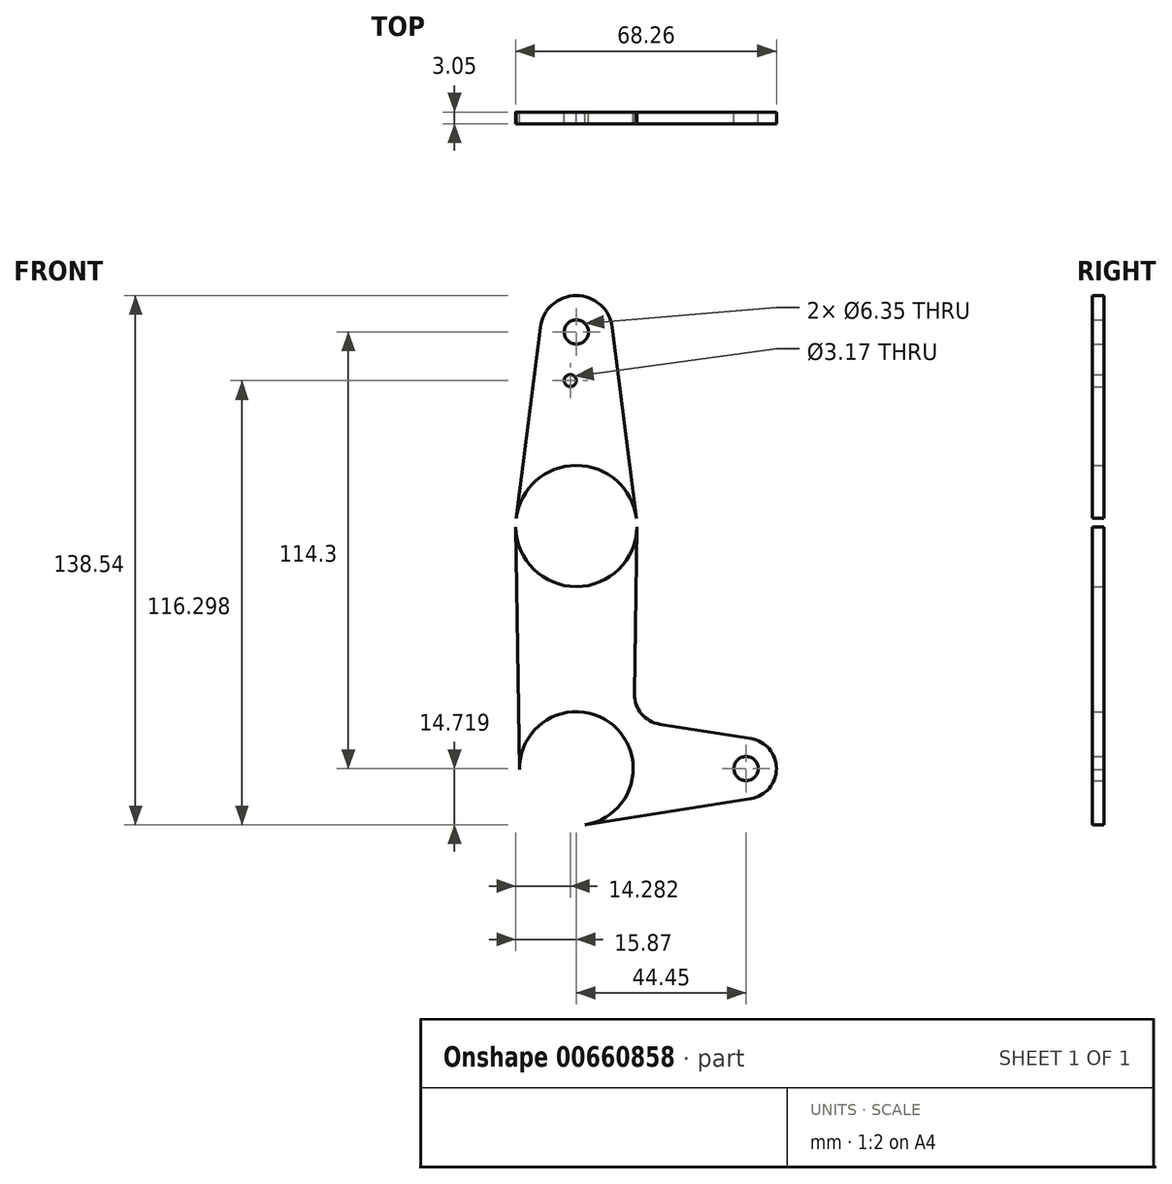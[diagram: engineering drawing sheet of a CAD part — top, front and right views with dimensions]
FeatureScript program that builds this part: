
annotation { "Feature Type Name" : "Feature", "Feature Type Description" : "" }
export const myFeature = defineFeature(function(context is Context, id is Id, definition is map)
    precondition{}
    {
        {
            var Q0;
            Q0=qCreatedBy(makeId("Front.planeOp"),FACE);
            var sketch = newSketch(context, id + "F0", { "sketchPlane" : qUnion([Q0])});
            skLineSegment(sketch, "E0", {"start": v(0, 0) * mm, "end": v(0, -57.23) * mm});
            skLineSegment(sketch, "E1", {"start": v(0, -57.23) * mm, "end": v(0, 57.07) * mm});
            skLineSegment(sketch, "E2", {"start": v(0, 57.07) * mm, "end": v(0, -57.23) * mm});
            skLineSegment(sketch, "E3", {"start": v(44.45, -57.23) * mm, "end": v(0, -57.23) * mm});
            skCircle(sketch, "E4", {"center": v(0, 6.27) * mm, "radius": 15.88 * mm});
            skCircle(sketch, "E5", {"center": v(0, 57.07) * mm, "radius": 9.53 * mm});
            skCircle(sketch, "E6", {"center": v(0, -57.23) * mm, "radius": 14.9 * mm});
            skCircle(sketch, "E7", {"center": v(44.45, -57.23) * mm, "radius": 7.94 * mm});
            skPoint(sketch, "E8.orphan", {"position": v(-60.31, 57.07) * mm});
            skLineSegment(sketch, "E9", {"start": v(9.45, 58.26) * mm, "end": v(15.75, 8.25) * mm});
            skLineSegment(sketch, "E10", {"start": v(15.87, 6.02) * mm, "end": v(15.2, -37.65) * mm});
            skLineSegment(sketch, "E11", {"start": v(-15.75, 8.25) * mm, "end": v(-9.45, 58.26) * mm});
            skLineSegment(sketch, "E12", {"start": v(-15.87, 6.02) * mm, "end": v(-14.9, -57.46) * mm});
            skLineSegment(sketch, "E13", {"start": v(45.7, -49.4) * mm, "end": v(21.9, -45.62) * mm});
            skLineSegment(sketch, "E14", {"start": v(2.33, -71.95) * mm, "end": v(45.7, -65.07) * mm});
            skCircle(sketch, "E15", {"center": v(0, 57.07) * mm, "radius": 3.18 * mm});
            skCircle(sketch, "E16", {"center": v(0, 6.27) * mm, "radius": 3.18 * mm});
            skCircle(sketch, "E17", {"center": v(0, -57.23) * mm, "radius": 3.18 * mm});
            skCircle(sketch, "E18", {"center": v(44.45, -57.23) * mm, "radius": 3.18 * mm});
            skCircle(sketch, "E19", {"center": v(-1.59, 44.35) * mm, "radius": 1.59 * mm});
            skArc(sketch, "E20.filletArc", {"start": v(15.2, -37.65) * mm, "mid": v(17.07, -42.88) * mm, "end": v(21.9, -45.62) * mm});
            skSolve(sketch);
        }
        {
            var Q0;
            {var subQ8=sQuery(id+"F0.wireOp",EDGE,"E10");Q0=makeQuery(id+"F0.imprint","IMPRINT",FACE,{"disambiguationData":[TD([[makeQuery(id+"F0.imprint","IMPRINT",EDGE,{"derivedFrom":subQ8}),-1.0]])]});}
            var Q1;
            {var subQ5=sQuery(id+"F0.wireOp",EDGE,"E14");Q1=makeQuery(id+"F0.imprint","IMPRINT",FACE,{"disambiguationData":[TD([[makeQuery(id+"F0.imprint","IMPRINT",EDGE,{"derivedFrom":subQ5}),1.0]])]});}
            var Q2;
            {var subQ0=sQuery(id+"F0.wireOp",EDGE,"E6");var subQ7=sQuery(id+"F0.wireOp",EDGE,"E2");var subQ8=makeQuery(id+"F0.imprint","INTERSECT",VERTEX,{"derivedFrom":[subQ7,subQ0]});Q2=makeQuery(id+"F0.imprint","IMPRINT",FACE,{"disambiguationData":[TD([[makeQuery(id+"F0.imprint","IMPRINT",EDGE,{"disambiguationData":[TD([[subQ8,-1.0]])],"derivedFrom":subQ7}),-1.0]])]});}
            var Q3;
            {var subQ0=sQuery(id+"F0.wireOp",EDGE,"E2");var subQ1=makeQuery(id+"F0.imprint","IMPRINT",VERTEX,{"derivedFrom":subQ0});Q3=makeQuery(id+"F0.imprint","IMPRINT",FACE,{"disambiguationData":[TD([[makeQuery(id+"F0.imprint","IMPRINT",EDGE,{"disambiguationData":[TD([[subQ1,1.0]])],"derivedFrom":subQ0}),1.0]])]});}
            var Q4;
            {var subQ2=sQuery(id+"F0.wireOp",EDGE,"E2");var subQ7=makeQuery(id+"F0.imprint","IMPRINT",VERTEX,{"derivedFrom":subQ2});Q4=makeQuery(id+"F0.imprint","IMPRINT",FACE,{"disambiguationData":[TD([[makeQuery(id+"F0.imprint","IMPRINT",EDGE,{"disambiguationData":[TD([[subQ7,1.0]])],"derivedFrom":subQ2}),-1.0]])]});}
            var Q5;
            {var subQ5=sQuery(id+"F0.wireOp",EDGE,"E12");Q5=makeQuery(id+"F0.imprint","IMPRINT",FACE,{"disambiguationData":[TD([[makeQuery(id+"F0.imprint","IMPRINT",EDGE,{"derivedFrom":subQ5}),1.0]])]});}
            var Q6;
            Q6=makeQuery(id+"F0.imprint","IMPRINT",FACE,{"disambiguationData":[TD([[makeQuery(id+"F0.imprint","IMPRINT",EDGE,{"derivedFrom":sQuery(id+"F0.wireOp",EDGE,"E18")}),-1.0]])]});
            var Q7;
            {var subQ0=sQuery(id+"F0.wireOp",EDGE,"E9");Q7=makeQuery(id+"F0.imprint","IMPRINT",FACE,{"disambiguationData":[TD([[makeQuery(id+"F0.imprint","IMPRINT",EDGE,{"derivedFrom":subQ0}),-1.0]])]});}
            var Q8;
            Q8=makeQuery(id+"F0.imprint","IMPRINT",FACE,{"disambiguationData":[TD([[makeQuery(id+"F0.imprint","IMPRINT",EDGE,{"derivedFrom":sQuery(id+"F0.wireOp",EDGE,"E15")}),-1.0]])]});
            var Q9;
            {var subQ0=sQuery(id+"F0.wireOp",EDGE,"E6");var subQ1=sQuery(id+"F0.wireOp",EDGE,"E2");var subQ2=makeQuery(id+"F0.imprint","INTERSECT",VERTEX,{"derivedFrom":[subQ1,subQ0]});Q9=makeQuery(id+"F0.imprint","IMPRINT",FACE,{"disambiguationData":[TD([[makeQuery(id+"F0.imprint","IMPRINT",EDGE,{"disambiguationData":[TD([[subQ2,-1.0]])],"derivedFrom":subQ1}),1.0]])]});}
            var Q10;
            {var subQ0=sQuery(id+"F0.wireOp",EDGE,"E2");var subQ1=makeQuery(id+"F0.imprint","IMPRINT",VERTEX,{"derivedFrom":subQ0});Q10=makeQuery(id+"F0.imprint","IMPRINT",FACE,{"disambiguationData":[TD([[makeQuery(id+"F0.imprint","IMPRINT",EDGE,{"disambiguationData":[TD([[subQ1,1.0]])],"derivedFrom":subQ0}),1.0]])]});}
            var Q11;
            {var subQ0=sQuery(id+"F0.wireOp",EDGE,"E9");Q11=makeQuery(id+"F0.imprint","IMPRINT",FACE,{"disambiguationData":[TD([[makeQuery(id+"F0.imprint","IMPRINT",EDGE,{"derivedFrom":subQ0}),-1.0]])]});}
            var Q12;
            Q12=makeQuery(id+"F0.imprint","IMPRINT",FACE,{"disambiguationData":[TD([[makeQuery(id+"F0.imprint","IMPRINT",EDGE,{"derivedFrom":sQuery(id+"F0.wireOp",EDGE,"E18")}),-1.0]])]});
            var Q13;
            {var subQ8=sQuery(id+"F0.wireOp",EDGE,"E10");Q13=makeQuery(id+"F0.imprint","IMPRINT",FACE,{"disambiguationData":[TD([[makeQuery(id+"F0.imprint","IMPRINT",EDGE,{"derivedFrom":subQ8}),-1.0]])]});}
            var Q14;
            {var subQ5=sQuery(id+"F0.wireOp",EDGE,"E12");Q14=makeQuery(id+"F0.imprint","IMPRINT",FACE,{"disambiguationData":[TD([[makeQuery(id+"F0.imprint","IMPRINT",EDGE,{"derivedFrom":subQ5}),1.0]])]});}
            var Q15;
            {var subQ2=sQuery(id+"F0.wireOp",EDGE,"E2");var subQ7=makeQuery(id+"F0.imprint","IMPRINT",VERTEX,{"derivedFrom":subQ2});Q15=makeQuery(id+"F0.imprint","IMPRINT",FACE,{"disambiguationData":[TD([[makeQuery(id+"F0.imprint","IMPRINT",EDGE,{"disambiguationData":[TD([[subQ7,1.0]])],"derivedFrom":subQ2}),-1.0]])]});}
            var Q16;
            {var subQ0=sQuery(id+"F0.wireOp",EDGE,"E6");var subQ7=sQuery(id+"F0.wireOp",EDGE,"E2");var subQ8=makeQuery(id+"F0.imprint","INTERSECT",VERTEX,{"derivedFrom":[subQ7,subQ0]});Q16=makeQuery(id+"F0.imprint","IMPRINT",FACE,{"disambiguationData":[TD([[makeQuery(id+"F0.imprint","IMPRINT",EDGE,{"disambiguationData":[TD([[subQ8,-1.0]])],"derivedFrom":subQ7}),-1.0]])]});}
            var Q17;
            Q17=makeQuery(id+"F0.imprint","IMPRINT",FACE,{"disambiguationData":[TD([[makeQuery(id+"F0.imprint","IMPRINT",EDGE,{"derivedFrom":sQuery(id+"F0.wireOp",EDGE,"E15")}),-1.0]])]});
            var Q18;
            {var subQ5=sQuery(id+"F0.wireOp",EDGE,"E14");Q18=makeQuery(id+"F0.imprint","IMPRINT",FACE,{"disambiguationData":[TD([[makeQuery(id+"F0.imprint","IMPRINT",EDGE,{"derivedFrom":subQ5}),1.0]])]});}
            var Q19;
            {var subQ0=sQuery(id+"F0.wireOp",EDGE,"E11");Q19=makeQuery(id+"F0.imprint","IMPRINT",FACE,{"disambiguationData":[TD([[makeQuery(id+"F0.imprint","IMPRINT",EDGE,{"derivedFrom":subQ0}),-1.0]])]});}
            var Q20;
            Q20 = qSketchRegion(id + "F2", true);
            extrude(context, id + "F1", {"entities" : qUnion([Q0, Q1, Q2, Q3, Q4, Q5, Q6, Q7, Q8, Q9, Q10, Q11, Q12, Q13, Q14, Q15, Q16, Q17, Q18, Q19, Q20]), "depth" : 3.05 * mm, "offsetDistance" : 25.4 * mm});
        }
    });
